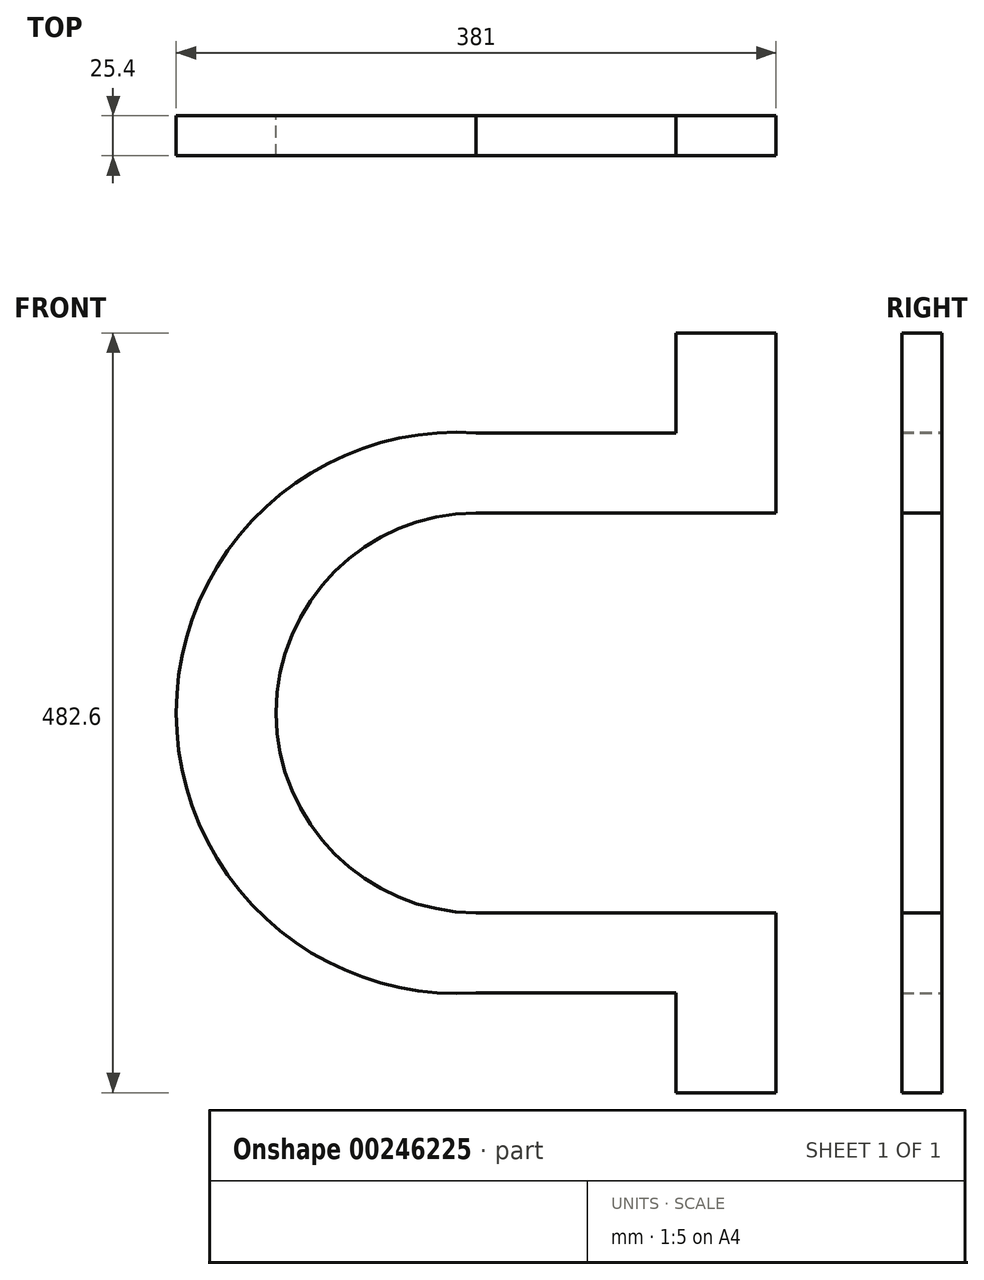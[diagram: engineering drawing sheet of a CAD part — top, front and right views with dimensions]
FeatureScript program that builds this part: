
annotation { "Feature Type Name" : "Feature", "Feature Type Description" : "" }
export const myFeature = defineFeature(function(context is Context, id is Id, definition is map)
    precondition{}
    {
        {
            var Q0;
            Q0=qCreatedBy(makeId("Front.planeOp"),FACE);
            var sketch = newSketch(context, id + "F0", { "sketchPlane" : qUnion([Q0])});
            skLineSegment(sketch, "E0.bottom", {"start": v(190.5, -177.8) * mm, "end": v(-24.55, -177.8) * mm});
            skLineSegment(sketch, "E0.top", {"start": v(190.5, 177.8) * mm, "end": v(-24.55, 177.8) * mm});
            skLineSegment(sketch, "E0.left", {"start": v(190.5, -177.8) * mm, "end": v(190.5, -127) * mm});
            skPoint(sketch, "E0.middle", {"position": v(0, 0) * mm});
            skArc(sketch, "E1", {"start": v(0, 127) * mm, "mid": v(-127, 0) * mm, "end": v(0, -127) * mm});
            skLineSegment(sketch, "E2", {"start": v(0, 127) * mm, "end": v(63.5, 127) * mm});
            skLineSegment(sketch, "E3", {"start": v(0, -127) * mm, "end": v(190.5, -127) * mm});
            skLineSegment(sketch, "E4", {"start": v(0, 127) * mm, "end": v(190.5, 127) * mm});
            skArc(sketch, "E5", {"start": v(0, 177.8) * mm, "mid": v(-190.5, 0) * mm, "end": v(0, -177.8) * mm});
            skPoint(sketch, "E5.second.point", {"position": v(-190.5, 0) * mm});
            skPoint(sketch, "E6.orphan", {"position": v(-190.5, 177.8) * mm});
            skPoint(sketch, "E7.orphan", {"position": v(-190.5, -177.8) * mm});
            skLineSegment(sketch, "E8.trimOffspring", {"start": v(190.5, 127) * mm, "end": v(190.5, 177.8) * mm});
            skLineSegment(sketch, "E9.bottom", {"start": v(190.5, 177.8) * mm, "end": v(127, 177.8) * mm});
            skLineSegment(sketch, "E9.top", {"start": v(190.5, 241.3) * mm, "end": v(127, 241.3) * mm});
            skLineSegment(sketch, "E9.left", {"start": v(190.5, 177.8) * mm, "end": v(190.5, 241.3) * mm});
            skLineSegment(sketch, "E9.right", {"start": v(127, 177.8) * mm, "end": v(127, 241.3) * mm});
            skPoint(sketch, "E9.middle", {"position": v(158.75, 209.55) * mm});
            skLineSegment(sketch, "E10.bottom", {"start": v(190.5, -177.8) * mm, "end": v(127, -177.8) * mm});
            skLineSegment(sketch, "E10.top", {"start": v(190.5, -241.3) * mm, "end": v(127, -241.3) * mm});
            skLineSegment(sketch, "E10.left", {"start": v(190.5, -177.8) * mm, "end": v(190.5, -241.3) * mm});
            skLineSegment(sketch, "E10.right", {"start": v(127, -177.8) * mm, "end": v(127, -241.3) * mm});
            skPoint(sketch, "E10.middle", {"position": v(158.75, -209.55) * mm});
            skSolve(sketch);
        }
        {
            var Q0;
            Q0 = qSketchRegion(id + "F0", true);
            extrude(context, id + "F1", {"entities" : qUnion([Q0]), "depth" : 25.4 * mm});
        }
    });
